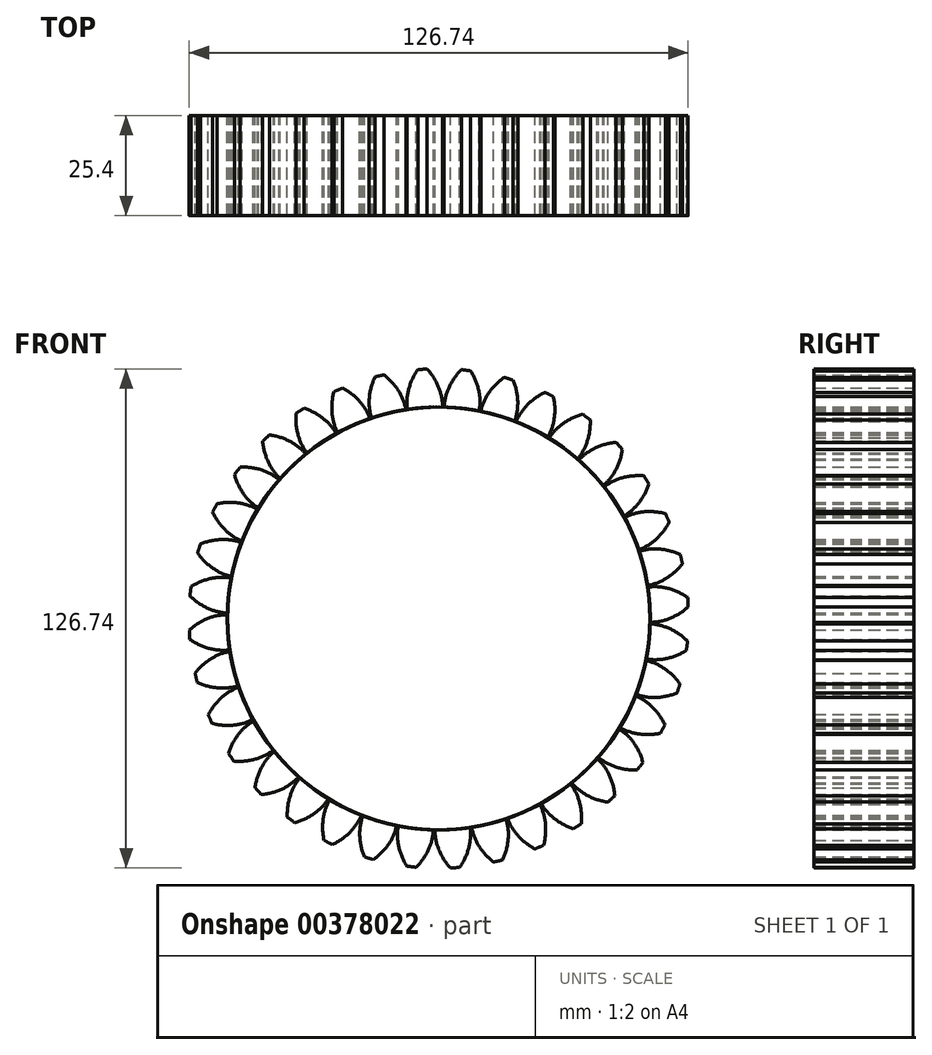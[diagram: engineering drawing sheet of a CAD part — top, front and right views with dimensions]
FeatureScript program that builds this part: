
annotation { "Feature Type Name" : "Feature", "Feature Type Description" : "" }
export const myFeature = defineFeature(function(context is Context, id is Id, definition is map)
    precondition{}
    {
        {
            var Q0;
            Q0=qCreatedBy(makeId("Front.planeOp"),FACE);
            var sketch = newSketch(context, id + "F0", { "sketchPlane" : qUnion([Q0])});
            skCircle(sketch, "E0", {"center": v(0, 0) * mm, "radius": 63.5 * mm, "construction": true});
            skCircle(sketch, "E1", {"center": v(0, 0) * mm, "radius": 58.67 * mm, "construction": true});
            skCircle(sketch, "E2", {"center": v(0, 0) * mm, "radius": 53.72 * mm});
            skLineSegment(sketch, "E3", {"start": v(0, 0) * mm, "end": v(0, 122.4) * mm, "construction": true});
            skLineSegment(sketch, "E4", {"start": v(0, 0) * mm, "end": v(-8.02, 122.4) * mm, "construction": true});
            skLineSegment(sketch, "E5", {"start": v(0, 58.67) * mm, "end": v(-89.7, 58.67) * mm, "construction": true});
            skLineSegment(sketch, "E6", {"start": v(0, 58.67) * mm, "end": v(-85.99, 27.38) * mm, "construction": true});
            skCircle(sketch, "E7", {"center": v(0, 0) * mm, "radius": 55.14 * mm, "construction": true});
            skCircle(sketch, "E8", {"center": v(0, 58.67) * mm, "radius": 14.6 * mm, "construction": true});
            skCircle(sketch, "E9", {"center": v(-13.63, 53.42) * mm, "radius": 14.6 * mm, "construction": true});
            skArc(sketch, "E10", {"start": v(0, 58.67) * mm, "mid": v(-1.28, 61.19) * mm, "end": v(-2.99, 63.43) * mm});
            skArc(sketch, "E11", {"start": v(0.97, 53.71) * mm, "mid": v(0.72, 56.24) * mm, "end": v(0, 58.67) * mm});
            skArc(sketch, "E12.MirrorCS", {"start": v(-7.66, 58.17) * mm, "mid": v(-6.72, 60.83) * mm, "end": v(-5.32, 63.28) * mm});
            skArc(sketch, "E13.MirrorCS", {"start": v(-7.98, 53.13) * mm, "mid": v(-8.06, 55.66) * mm, "end": v(-7.66, 58.17) * mm});
            skArc(sketch, "E14", {"start": v(-5.32, 63.28) * mm, "mid": v(-4.13, 63.32) * mm, "end": v(-2.94, 63.37) * mm});
            skSolve(sketch);
        }
        {
            var Q0;
            {var subQ0=sQuery(id+"F0.wireOp",EDGE,"E2");var subQ1=makeQuery(id+"F0.imprint","INTERSECT",VERTEX,{"derivedFrom":[subQ0,sQuery(id+"F0.wireOp",EDGE,"E11")]});Q0=makeQuery(id+"F0.imprint","IMPRINT",FACE,{"disambiguationData":[TD([[makeQuery(id+"F0.imprint","IMPRINT",EDGE,{"disambiguationData":[TD([[subQ1,-1.0]])],"derivedFrom":subQ0}),1.0]])]});}
            var Q1;
            {var subQ0=sQuery(id+"F0.wireOp",EDGE,"E11");Q1=makeQuery(id+"F0.imprint","IMPRINT",FACE,{"disambiguationData":[TD([[makeQuery(id+"F0.imprint","IMPRINT",EDGE,{"derivedFrom":subQ0}),1.0]])]});}
            extrude(context, id + "F1", {"entities" : qUnion([Q0, Q1]), "endBound" : BoundingType.SYMMETRIC, "depth" : 25.4 * mm});
        }
        {
            var Q0;
            Q0=makeQuery(id+"F1.opExtrude","SWEPT_BODY",BODY,{"disambiguationData":[OSD([sQuery(id+"F0.wireOp",EDGE,"E2"),sQuery(id+"F0.wireOp",EDGE,"E10"),sQuery(id+"F0.wireOp",EDGE,"E11"),sQuery(id+"F0.wireOp",EDGE,"E12.MirrorCS"),sQuery(id+"F0.wireOp",EDGE,"E13.MirrorCS"),sQuery(id+"F0.wireOp",EDGE,"E14")])]});
            var Q1;
            Q1=makeQuery(id+"F1.opExtrude","SWEPT_FACE",FACE,{"disambiguationData":[OSD([sQuery(id+"F0.wireOp",EDGE,"E2")])]});
            circularPattern(context, id + "F2", {"entities" : qUnion([Q0]), "axis" : qUnion([Q1]), "angle" : 360 * degree, "instanceCount" : 36, "equalSpace" : true});
        }
    });
